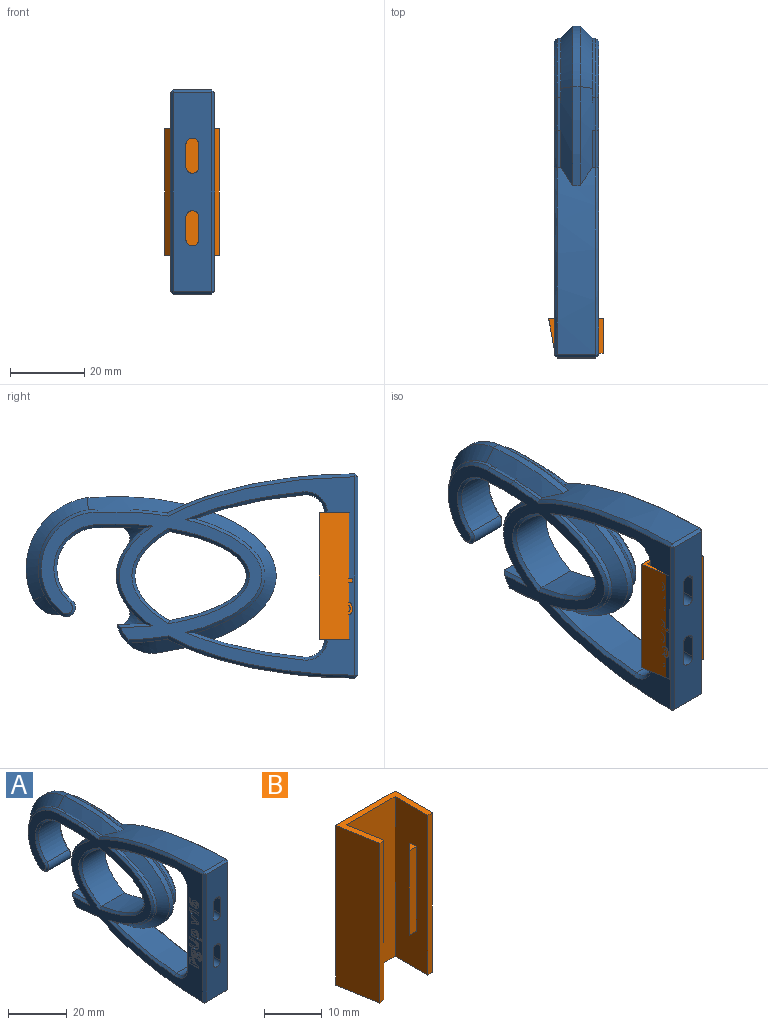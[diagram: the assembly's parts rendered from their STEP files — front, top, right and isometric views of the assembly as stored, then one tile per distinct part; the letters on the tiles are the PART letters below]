
ASSEMBLY  parts=2 mates=1
PART A: 284 faces, bbox 13x92.1x56.1 mm
  f0: plane 85.41x54.41mm, normal (-1,0,0), area 1114.5mm2, adj f78,f79,f80,f81,f82,f83,f84,f85
  f1: cylinder r=16mm len=28.43mm, axis (-1,0,0), area 47.1mm2, adj f12,f14,f65,f66,f70,f76,f105
  f2: extruded ~10.08x1.04mm, area 9.1mm2, adj f14,f16,f70,f101
  f3: extruded ~10.91x4.2mm, area 19mm2, adj f17,f19,f62,f63,f100
  f4: extruded ~30.7x18.87mm, area 61.6mm2, adj f8,f11,f48,f114
  f5: plane 33.72x10.4mm, normal (0,1,0), area 99mm2, adj f9,f10,f35,f37,f38,f39,f40,f41
  f6: plane 53.4x10.4mm, normal (0,-1,0), area 494.1mm2, adj f27,f28,f29,f30,f31,f32,f33,f34
  f7: extruded ~24x11.2mm, area 354.4mm2, adj f25,f26,f122
  f8: extruded ~29.4x10.4mm, area 288mm2, adj f4,f9,f23,f47,f48,f49,f115,f119
  f9: cylinder r=5mm len=10.4mm, axis (-1,0,0), area 85.2mm2, adj f5,f8,f43,f113,f121
  f10: cylinder r=5mm len=10.4mm, axis (-1,0,0), area 85.2mm2, adj f5,f11,f36,f110,f118
  f11: extruded ~29.4x10.4mm, area 288mm2, adj f4,f10,f23,f47,f48,f49,f112,f116
  f12: cylinder r=2.5mm len=10.4mm, axis (-1,0,0), area 81.7mm2, adj f1,f13,f24,f72,f81,f107
  f13: cylinder r=16mm len=28.43mm, axis (-1,0,0), area 47.1mm2, adj f12,f14,f67,f68,f71,f77,f83
  f14: plane 10.41x8.77mm, normal (0,0,1), area 80.5mm2, adj f1,f2,f13,f15,f70,f71,f75,f85
  f15: extruded ~10.08x1.04mm, area 9.1mm2, adj f14,f16,f71,f87
  f16: extruded ~50.36x10.53mm, area 511.9mm2, adj f2,f15,f69,f70,f71,f90,f95,f99
  f17: extruded ~50.36x10.53mm, area 511.8mm2, adj f3,f18,f60,f62,f64,f88,f93,f98
  f18: extruded ~10.91x4.2mm, area 19mm2, adj f17,f19,f60,f61,f86
  f19: cylinder r=9.71mm len=10.76mm, axis (-1,0,0), area 76.6mm2, adj f3,f18,f20,f61,f63,f64,f84,f102
  f20: extruded ~10.4x7.29mm, area 38.9mm2, adj f19,f21,f55,f56,f57,f58,f59,f82
  f21: extruded ~25.66x10.4mm, area 250.9mm2, adj f20,f22,f50,f51,f52,f53,f54,f55
  f22: extruded ~13.86x10.4mm, area 107.3mm2, adj f21,f24,f50,f51,f52,f53,f54,f78
  f23: extruded ~30.7x18.87mm, area 61.6mm2, adj f8,f11,f47,f117
  f24: cylinder r=11mm len=19.46mm, axis (-1,0,0), area 267.4mm2, adj f12,f22,f79,f109
  f25: extruded ~24x20.76mm, area 570.7mm2, adj f7,f26,f123
  f26: plane 85.41x54.41mm, normal (1,0,0), area 1216.5mm2, adj f7,f25,f94,f98,f99,f100,f101,f102
  f27: cylinder r=1.75mm len=6mm, axis (0,-1,0), area 33mm2, adj f6,f28,f30,f44
  f28: plane 6x6mm, normal (1,0,0), area 36mm2, adj f6,f27,f29,f42
  f29: cylinder r=1.75mm len=6mm, axis (0,-1,0), area 33mm2, adj f6,f28,f30,f41,f43,f45
  f30: plane 6x6mm, normal (-1,0,0), area 36mm2, adj f6,f27,f29,f46
  f31: plane 6x6mm, normal (-1,0,0), area 36mm2, adj f6,f32,f34,f40
  f32: cylinder r=1.75mm len=6mm, axis (0,-1,0), area 33mm2, adj f6,f31,f33,f35,f36,f38
  f33: plane 6x6mm, normal (1,0,0), area 36mm2, adj f6,f32,f34,f37
  f34: cylinder r=1.75mm len=6mm, axis (0,-1,0), area 33mm2, adj f6,f31,f33,f39
  f35: cone r=4.75mm half-angle=45deg, axis (0,1,0), area 14.4mm2, adj f5,f32,f36,f37
  f36: bspline ~4.77x3.13mm, area 13.8mm2, adj f10,f32,f35,f38
  f37: plane 6x3mm, normal (0.71,0.71,0), area 25.5mm2, adj f5,f33,f35,f39
  f38: cone r=4.75mm half-angle=45deg, axis (0,1,0), area 14.4mm2, adj f5,f32,f36,f40
  f39: cone r=4.75mm half-angle=45deg, axis (0,1,0), area 43.3mm2, adj f5,f34,f37,f40
  f40: plane 6x3mm, normal (-0.71,0.71,0), area 25.5mm2, adj f5,f31,f38,f39
  f41: cone r=4.75mm half-angle=45deg, axis (0,1,0), area 14.4mm2, adj f5,f29,f42,f43
  f42: plane 6x3mm, normal (0.71,0.71,0), area 25.5mm2, adj f5,f28,f41,f44
  f43: bspline ~4.77x3.13mm, area 13.8mm2, adj f9,f29,f41,f45
  f44: cone r=4.75mm half-angle=45deg, axis (0,1,0), area 43.3mm2, adj f5,f27,f42,f46
  f45: cone r=4.75mm half-angle=45deg, axis (0,1,0), area 14.4mm2, adj f5,f29,f43,f46
  f46: plane 6x3mm, normal (-0.71,0.71,0), area 25.5mm2, adj f5,f30,f44,f45
  f47: bspline ~40.67x32.57mm, area 230mm2, adj f8,f11,f23,f49
  f48: bspline ~40.67x32.57mm, area 230mm2, adj f4,f8,f11,f49
  f49: extruded ~34.16x17.06mm, area 102.3mm2, adj f8,f11,f47,f48
  f50: cone r=3mm half-angle=45deg, axis (1,0,0), area 12.9mm2, adj f21,f22,f51,f54
  f51: plane 0.41x0.27mm, normal (1,0,0), area 0.1mm2, adj f21,f22,f50
  f52: cone r=7mm half-angle=45deg, axis (-1,0,0), area 12.9mm2, adj f21,f22,f53,f54
  f53: plane 0.41x0.27mm, normal (-1,0,0), area 0.1mm2, adj f21,f22,f52
  f54: cylinder r=3mm len=4.8mm, axis (-1,0,0), area 13.2mm2, adj f21,f22,f50,f52
  f55: cone r=3mm half-angle=45deg, axis (1,0,0), area 12.9mm2, adj f20,f21,f56,f59
  f56: plane 0.41x0.27mm, normal (1,0,0), area 0.1mm2, adj f20,f21,f55
  f57: cone r=7mm half-angle=45deg, axis (-1,0,0), area 12.9mm2, adj f20,f21,f58,f59
  f58: plane 0.41x0.27mm, normal (-1,0,0), area 0.1mm2, adj f20,f21,f57
  f59: cylinder r=3mm len=4.8mm, axis (-1,0,0), area 13.2mm2, adj f20,f21,f55,f57
  f60: bspline ~14.46x6.99mm, area 25.7mm2, adj f17,f18,f61,f64
  f61: cone r=9.71mm half-angle=45deg, axis (1,0,0), area 18.1mm2, adj f18,f19,f60
  f62: bspline ~14.46x6.99mm, area 25.7mm2, adj f3,f17,f63,f64
  f63: cone r=5.71mm half-angle=45deg, axis (-1,0,0), area 18.1mm2, adj f3,f19,f62
  f64: extruded ~7.7x2mm, area 15.7mm2, adj f17,f19,f60,f62
  f65: cone r=15.27mm half-angle=45deg, axis (-1,0,0), area 153mm2, adj f1,f66,f70,f74
  f66: cone r=3mm half-angle=45deg, axis (-1,0,0), area 22.6mm2, adj f1,f65,f73,f76
  f67: cone r=19.27mm half-angle=45deg, axis (1,0,0), area 153mm2, adj f13,f68,f71,f74
  f68: cone r=7mm half-angle=45deg, axis (1,0,0), area 22.6mm2, adj f13,f67,f73,f77
  f69: extruded ~26.57x2.12mm, area 53.5mm2, adj f16,f70,f71,f74
  f70: bspline ~38.15x7.96mm, area 112.2mm2, adj f1,f2,f14,f16,f65,f69,f75
  f71: bspline ~38.15x7.96mm, area 112.2mm2, adj f13,f14,f15,f16,f67,f69,f75
  f72: plane 2x0.93mm, normal (0,0,-1), area 1.9mm2, adj f12,f73,f76,f77
  f73: cylinder r=7mm len=6.28mm, axis (-1,0,0), area 15.6mm2, adj f66,f68,f72,f74
  f74: cylinder r=19.27mm len=27.58mm, axis (-1,0,0), area 72.4mm2, adj f65,f67,f69,f73
  f75: extruded ~8.66x7.52mm, area 65.2mm2, adj f14,f70,f71
  f76: plane 0.95x0.83mm, normal (0.71,0,-0.71), area 0.5mm2, adj f1,f66,f72
  f77: plane 0.95x0.83mm, normal (-0.71,0,-0.71), area 0.5mm2, adj f13,f68,f72
  f78: bspline ~16.07x1.3mm, area 16.9mm2, adj f0,f22,f79,f80
  f79: cone r=11.8mm half-angle=45deg, axis (-1,0,0), area 30.2mm2, adj f0,f24,f78,f81
  f80: bspline ~30.07x11.02mm, area 36.3mm2, adj f0,f21,f78,f82
  f81: cone r=2.5mm half-angle=45deg, axis (1,0,0), area 7.5mm2, adj f0,f12,f79,f83
  f82: bspline ~10.35x1.36mm, area 8.9mm2, adj f0,f20,f80,f84
  f83: cone r=16mm half-angle=45deg, axis (1,0,0), area 43.4mm2, adj f0,f13,f81,f85
  f84: cone r=9.71mm half-angle=45deg, axis (1,0,0), area 5.4mm2, adj f0,f19,f82,f86
  f85: plane 8.76x0.8mm, normal (-0.71,0,0.71), area 9.9mm2, adj f0,f14,f83,f87
  f86: bspline ~11.21x1.9mm, area 12.3mm2, adj f0,f18,f84,f88
  f87: bspline ~10.39x1.87mm, area 11.6mm2, adj f0,f15,f85,f90
  f88: bspline ~55.49x12.73mm, area 58.6mm2, adj f0,f17,f86,f91
  f89: plane 53.4x0.8mm, normal (-0.71,-0.71,0), area 60.4mm2, adj f0,f6,f91,f92
  f90: bspline ~55.49x12.73mm, area 58.6mm2, adj f0,f16,f87,f92
  f91: plane 0.8x0.8mm, normal (-0.58,-0.58,-0.58), area 0.6mm2, adj f88,f89,f93
  f92: plane 0.8x0.8mm, normal (-0.58,-0.58,0.58), area 0.6mm2, adj f89,f90,f95
  f93: plane 10.4x0.8mm, normal (0,-0.71,-0.71), area 11.8mm2, adj f6,f17,f91,f96
  f94: plane 53.4x0.8mm, normal (0.71,-0.71,0), area 60.4mm2, adj f6,f26,f96,f97
  f95: plane 10.4x0.8mm, normal (0,-0.71,0.71), area 11.8mm2, adj f6,f16,f92,f97
  f96: plane 0.8x0.8mm, normal (0.58,-0.58,-0.58), area 0.6mm2, adj f93,f94,f98
  f97: plane 0.8x0.8mm, normal (0.58,-0.58,0.58), area 0.6mm2, adj f94,f95,f99
  f98: bspline ~55.49x12.73mm, area 58.6mm2, adj f17,f26,f96,f100
  f99: bspline ~55.49x12.73mm, area 58.6mm2, adj f16,f26,f97,f101
  f100: bspline ~11.21x1.9mm, area 12.3mm2, adj f3,f26,f98,f102
  f101: bspline ~10.39x1.87mm, area 11.6mm2, adj f2,f26,f99,f103
  f102: cone r=8.91mm half-angle=45deg, axis (-1,0,0), area 5.4mm2, adj f19,f26,f100,f104
  f103: plane 8.76x0.8mm, normal (0.71,0,0.71), area 9.9mm2, adj f14,f26,f101,f105
  f104: bspline ~9.42x1.3mm, area 8.9mm2, adj f20,f26,f102,f106
  f105: cone r=15.2mm half-angle=45deg, axis (-1,0,0), area 43.4mm2, adj f1,f26,f103,f107
  f106: bspline ~30.07x11.02mm, area 36.3mm2, adj f21,f26,f104,f108
  f107: cone r=1.7mm half-angle=45deg, axis (-1,0,0), area 7.5mm2, adj f12,f26,f105,f109
  f108: bspline ~16.07x1.3mm, area 16.9mm2, adj f22,f26,f106,f109
  f109: cone r=11mm half-angle=45deg, axis (1,0,0), area 30.2mm2, adj f24,f26,f107,f108
  f110: cone r=5mm half-angle=45deg, axis (1,0,0), area 10.2mm2, adj f10,f26,f111,f112
  f111: plane 33.72x0.8mm, normal (0.71,0.71,0), area 38.1mm2, adj f5,f26,f110,f113
  f112: bspline ~31.88x8.19mm, area 35.6mm2, adj f11,f26,f110,f114
  f113: cone r=5.8mm half-angle=45deg, axis (1,0,0), area 10.2mm2, adj f9,f26,f111,f115
  f114: bspline ~31.9x21.32mm, area 60mm2, adj f4,f26,f112,f115
  f115: bspline ~33.39x8.89mm, area 35.7mm2, adj f8,f26,f113,f114
  f116: bspline ~33.36x8.88mm, area 35.6mm2, adj f0,f11,f117,f118
  f117: bspline ~33.07x23.99mm, area 60mm2, adj f0,f23,f116,f119
  f118: cone r=5.8mm half-angle=45deg, axis (-1,0,0), area 10.2mm2, adj f0,f10,f116,f120
  f119: bspline ~33.39x8.89mm, area 35.7mm2, adj f0,f8,f117,f121
  f120: plane 33.72x0.8mm, normal (-0.71,0.71,0), area 38.1mm2, adj f0,f5,f118,f121
  f121: cone r=5mm half-angle=45deg, axis (-1,0,0), area 10.2mm2, adj f0,f9,f119,f120
  f122: bspline ~27.31x11.74mm, area 37.1mm2, adj f0,f7,f123
  f123: bspline ~26.44x24.47mm, area 59.3mm2, adj f0,f25,f122
  f124: plane 2.89x0.3mm, normal (0,0,-1), area 0.9mm2, adj f0,f125,f138,f139
  f125: plane 0.94x0.3mm, normal (0,-1,0), area 0.3mm2, adj f0,f124,f126,f139
  f126: plane 2.73x0.3mm, normal (0,0,1), area 0.8mm2, adj f0,f125,f127,f139
  f127: extruded ~0.76x0.3mm, area 0.2mm2, adj f0,f126,f128,f139
  f128: extruded ~0.67x0.3mm, area 0.2mm2, adj f0,f127,f129,f139
  f129: extruded ~0.69x0.3mm, area 0.2mm2, adj f0,f128,f130,f139
  f130: extruded ~0.76x0.3mm, area 0.2mm2, adj f0,f129,f131,f139
  f131: plane 2.73x0.3mm, normal (0,0,-1), area 0.8mm2, adj f0,f130,f132,f139
  f132: plane 0.94x0.3mm, normal (0,-1,0), area 0.3mm2, adj f0,f131,f133,f139
  f133: plane 2.88x0.3mm, normal (0,0,1), area 0.9mm2, adj f0,f132,f134,f139
  f134: extruded ~1.21x0.48mm, area 0.4mm2, adj f0,f133,f135,f139
  f135: extruded ~1.34x0.44mm, area 0.4mm2, adj f0,f134,f136,f139
  f136: extruded ~0.99x0.3mm, area 0.3mm2, adj f0,f135,f137,f139
  f137: extruded ~0.64x0.57mm, area 0.3mm2, adj f0,f136,f138,f139
  f138: extruded ~0.87x0.3mm, area 0.3mm2, adj f0,f124,f137,f139
  f139: plane 4.52x3.66mm, normal (-1,0,0), area 9.1mm2, adj f124,f125,f126,f127,f128,f129,f130,f131
  f140: extruded ~0.44x0.3mm, area 0.1mm2, adj f141,f183,f184,f276
  f141: extruded ~0.62x0.51mm, area 0.3mm2, adj f140,f142,f184,f276
  f142: extruded ~0.62x0.51mm, area 0.3mm2, adj f141,f143,f184,f276
  f143: extruded ~0.44x0.3mm, area 0.1mm2, adj f142,f144,f184,f276
  f144: extruded ~0.38x0.3mm, area 0.1mm2, adj f143,f183,f184,f276
  f145: extruded ~0.3x0.3mm, area 0.1mm2, adj f146,f181,f184,f185
  f146: extruded ~0.32x0.3mm, area 0.1mm2, adj f145,f147,f184,f185
  f147: extruded ~0.43x0.3mm, area 0.1mm2, adj f146,f148,f184,f185
  f148: plane 0.48x0.3mm, normal (0,1,0), area 0.1mm2, adj f147,f149,f184,f185
  f149: extruded ~0.52x0.3mm, area 0.2mm2, adj f148,f150,f184,f185
  f150: extruded ~0.3x0.27mm, area 0.1mm2, adj f149,f151,f184,f185
  f151: extruded ~0.38x0.3mm, area 0.1mm2, adj f150,f152,f184,f185
  f152: extruded ~0.78x0.3mm, area 0.2mm2, adj f151,f181,f184,f185
  f153: plane 0.47x0.3mm, normal (0,0,-1), area 0.1mm2, adj f0,f154,f182,f184
  f154: plane 1.19x0.3mm, normal (0,-1,0), area 0.4mm2, adj f0,f153,f155,f184
  f155: extruded ~0.3x0.25mm, area 0.1mm2, adj f0,f154,f156,f184
  f156: extruded ~0.34x0.3mm, area 0.1mm2, adj f0,f155,f157,f184
  f157: extruded ~1.04x0.31mm, area 0.3mm2, adj f0,f156,f158,f184
  f158: extruded ~0.86x0.36mm, area 0.3mm2, adj f0,f157,f159,f184
  f159: extruded ~0.61x0.3mm, area 0.2mm2, adj f0,f158,f160,f184
  f160: extruded ~0.43x0.37mm, area 0.2mm2, adj f0,f159,f161,f184
  f161: extruded ~0.33x0.3mm, area 0.1mm2, adj f0,f160,f162,f184
  f162: extruded ~0.32x0.3mm, area 0.1mm2, adj f0,f161,f163,f184
  f163: extruded ~0.3x0.3mm, area 0.1mm2, adj f0,f162,f164,f184
  f164: extruded ~0.3x0.25mm, area 0.1mm2, adj f0,f163,f165,f184
  f165: extruded ~0.56x0.3mm, area 0.2mm2, adj f0,f164,f166,f184
  f166: extruded ~0.52x0.3mm, area 0.2mm2, adj f0,f165,f167,f184
  f167: extruded ~0.7x0.38mm, area 0.2mm2, adj f0,f166,f168,f184
  f168: extruded ~1.09x0.3mm, area 0.3mm2, adj f0,f167,f169,f184
  f169: extruded ~1.43x0.33mm, area 0.4mm2, adj f0,f168,f170,f184
  f170: extruded ~0.93x0.5mm, area 0.3mm2, adj f0,f169,f171,f184
  f171: extruded ~0.71x0.3mm, area 0.2mm2, adj f0,f170,f172,f184
  f172: extruded ~0.86x0.3mm, area 0.3mm2, adj f0,f171,f173,f184
  f173: plane 0.58x0.3mm, normal (0,-1,0), area 0.2mm2, adj f0,f172,f174,f184
  f174: extruded ~0.51x0.3mm, area 0.2mm2, adj f0,f173,f175,f184
  f175: extruded ~0.3x0.24mm, area 0.1mm2, adj f0,f174,f176,f184
  f176: plane 0.3x0.14mm, normal (0,0.99,0.11), area 0mm2, adj f0,f175,f177,f184
  f177: plane 0.3x0.17mm, normal (0,1,0.06), area 0.1mm2, adj f0,f176,f178,f184
  f178: extruded ~1.06x0.31mm, area 0.3mm2, adj f0,f177,f179,f184
  f179: extruded ~0.86x0.38mm, area 0.3mm2, adj f0,f178,f180,f184
  f180: extruded ~0.51x0.3mm, area 0.2mm2, adj f0,f179,f182,f184
  f181: extruded ~0.52x0.3mm, area 0.2mm2, adj f145,f152,f184,f185
  f182: plane 0.53x0.3mm, normal (0,0.97,-0.25), area 0.2mm2, adj f0,f153,f180,f184
  f183: extruded ~0.39x0.3mm, area 0.1mm2, adj f140,f144,f184,f276
  f184: plane 4.98x3.44mm, normal (-1,0,0), area 10.1mm2, adj f140,f141,f142,f143,f144,f145,f146,f147
  f185: plane 1.77x0.85mm, normal (-1,0,0), area 1.3mm2, adj f145,f146,f147,f148,f149,f150,f151,f152
  f186: extruded ~0.46x0.3mm, area 0.2mm2, adj f187,f210,f211,f277
  f187: extruded ~0.48x0.3mm, area 0.2mm2, adj f186,f188,f211,f277
  f188: extruded ~0.61x0.3mm, area 0.2mm2, adj f187,f189,f211,f277
  f189: extruded ~0.43x0.3mm, area 0.1mm2, adj f188,f190,f211,f277
  f190: extruded ~0.49x0.3mm, area 0.2mm2, adj f189,f191,f211,f277
  f191: extruded ~0.46x0.3mm, area 0.2mm2, adj f190,f192,f211,f277
  f192: extruded ~0.51x0.3mm, area 0.2mm2, adj f191,f210,f211,f277
  f193: extruded ~1.97x0.56mm, area 0.6mm2, adj f0,f194,f209,f211
  f194: extruded ~1.06x0.3mm, area 0.3mm2, adj f0,f193,f195,f211
  f195: extruded ~0.67x0.57mm, area 0.3mm2, adj f0,f194,f196,f211
  f196: extruded ~0.86x0.3mm, area 0.3mm2, adj f0,f195,f197,f211
  f197: extruded ~1.12x0.42mm, area 0.4mm2, adj f0,f196,f198,f211
  f198: extruded ~1.13x0.4mm, area 0.4mm2, adj f0,f197,f199,f211
  f199: extruded ~1.04x0.34mm, area 0.3mm2, adj f0,f198,f200,f211
  f200: extruded ~0.94x0.38mm, area 0.3mm2, adj f0,f199,f201,f211
  f201: extruded ~0.97x0.52mm, area 0.3mm2, adj f0,f200,f202,f211
  f202: plane 0.3x0.04mm, normal (0,-1,0), area 0mm2, adj f0,f201,f203,f211
  f203: extruded ~0.81x0.3mm, area 0.3mm2, adj f0,f202,f204,f211
  f204: extruded ~0.46x0.43mm, area 0.2mm2, adj f0,f203,f205,f211
  f205: extruded ~0.79x0.3mm, area 0.2mm2, adj f0,f204,f206,f211
  f206: extruded ~0.54x0.3mm, area 0.2mm2, adj f0,f205,f207,f211
  f207: plane 0.75x0.3mm, normal (0,0,-1), area 0.2mm2, adj f0,f206,f208,f211
  f208: extruded ~0.6x0.3mm, area 0.2mm2, adj f0,f207,f209,f211
  f209: extruded ~1.68x0.65mm, area 0.6mm2, adj f0,f193,f208,f211
  f210: extruded ~0.58x0.3mm, area 0.2mm2, adj f186,f192,f211,f277
  f211: plane 4.58x3.15mm, normal (-1,0,0), area 8.5mm2, adj f186,f187,f188,f189,f190,f191,f192,f193
  f212: extruded ~0.5x0.3mm, area 0.2mm2, adj f213,f234,f235,f278
  f213: extruded ~0.48x0.3mm, area 0.2mm2, adj f212,f214,f235,f278
  f214: extruded ~0.76x0.3mm, area 0.2mm2, adj f213,f215,f235,f278
  f215: extruded ~1.03x0.63mm, area 0.4mm2, adj f214,f216,f235,f278
  f216: extruded ~0.52x0.3mm, area 0.2mm2, adj f215,f217,f235,f278
  f217: extruded ~0.79x0.3mm, area 0.2mm2, adj f216,f218,f235,f278
  f218: plane 0.3x0.1mm, normal (0,0,-1), area 0mm2, adj f217,f234,f235,f278
  f219: extruded ~0.94x0.44mm, area 0.3mm2, adj f0,f220,f233,f235
  f220: extruded ~0.7x0.3mm, area 0.2mm2, adj f0,f219,f221,f235
  f221: extruded ~0.61x0.46mm, area 0.2mm2, adj f0,f220,f222,f235
  f222: extruded ~0.95x0.3mm, area 0.3mm2, adj f0,f221,f223,f235
  f223: extruded ~1.3x0.34mm, area 0.4mm2, adj f0,f222,f224,f235
  f224: extruded ~0.95x0.47mm, area 0.3mm2, adj f0,f223,f225,f235
  f225: extruded ~0.97x0.51mm, area 0.3mm2, adj f0,f224,f226,f235
  f226: plane 0.3x0.04mm, normal (0,-1,0), area 0mm2, adj f0,f225,f227,f235
  f227: plane 0.44x0.3mm, normal (0,-0.28,-0.96), area 0.1mm2, adj f0,f226,f228,f235
  f228: plane 0.76x0.3mm, normal (0,-1,0), area 0.2mm2, adj f0,f227,f229,f235
  f229: plane 4.91x0.3mm, normal (0,0,1), area 1.5mm2, adj f0,f228,f230,f235
  f230: plane 0.93x0.3mm, normal (0,1,0), area 0.3mm2, adj f0,f229,f231,f235
  f231: plane 1.38x0.3mm, normal (0,0,-1), area 0.4mm2, adj f0,f230,f232,f235
  f232: extruded ~0.49x0.3mm, area 0.1mm2, adj f0,f231,f233,f235
  f233: plane 0.3x0.05mm, normal (0,1,0), area 0mm2, adj f0,f219,f232,f235
  f234: extruded ~0.7x0.3mm, area 0.2mm2, adj f212,f218,f235,f278
  f235: plane 4.98x3.19mm, normal (-1,0,0), area 9.1mm2, adj f212,f213,f214,f215,f216,f217,f218,f219
  f236: extruded ~1.1x0.45mm, area 0.4mm2, adj f0,f237,f251,f252
  f237: extruded ~1.04x0.42mm, area 0.3mm2, adj f0,f236,f238,f252
  f238: extruded ~1.24x0.35mm, area 0.4mm2, adj f0,f237,f239,f252
  f239: plane 1.43x0.3mm, normal (0,-1,0), area 0.4mm2, adj f0,f238,f240,f252
  f240: plane 4.46x0.3mm, normal (0,0,1), area 1.3mm2, adj f0,f239,f241,f252
  f241: plane 0.95x0.3mm, normal (0,1,0), area 0.3mm2, adj f0,f240,f242,f252
  f242: plane 1.59x0.3mm, normal (0,0,-1), area 0.5mm2, adj f0,f241,f243,f252
  f243: plane 0.41x0.3mm, normal (0,1,0), area 0.1mm2, adj f0,f242,f251,f252
  f244: plane 0.31x0.3mm, normal (0,-1,0), area 0.1mm2, adj f245,f250,f252,f253
  f245: plane 1.32x0.3mm, normal (0,0,-1), area 0.4mm2, adj f244,f246,f252,f253
  f246: plane 0.43x0.3mm, normal (0,1,0), area 0.1mm2, adj f245,f247,f252,f253
  f247: extruded ~0.57x0.3mm, area 0.2mm2, adj f246,f248,f252,f253
  f248: extruded ~0.49x0.3mm, area 0.2mm2, adj f247,f249,f252,f253
  f249: extruded ~0.5x0.3mm, area 0.2mm2, adj f248,f250,f252,f253
  f250: extruded ~0.65x0.3mm, area 0.2mm2, adj f244,f249,f252,f253
  f251: extruded ~1.28x0.38mm, area 0.4mm2, adj f0,f236,f243,f252
  f252: plane 4.46x3.08mm, normal (-1,0,0), area 8.1mm2, adj f236,f237,f238,f239,f240,f241,f242,f243
  f253: plane 1.32x1.18mm, normal (-1,0,0), area 1.4mm2, adj f244,f245,f246,f247,f248,f249,f250
  f254: plane 0.94x0.3mm, normal (0,1,0), area 0.3mm2, adj f0,f255,f263,f264
  f255: plane 4.46x0.3mm, normal (0,0,-1), area 1.3mm2, adj f0,f254,f256,f264
  f256: plane 0.78x0.3mm, normal (0,-1,0), area 0.2mm2, adj f0,f255,f257,f264
  f257: plane 1.44x1.14mm, normal (0,-0.78,0.62), area 0.6mm2, adj f0,f256,f258,f264
  f258: plane 0.57x0.46mm, normal (0,0.63,0.78), area 0.2mm2, adj f0,f257,f259,f264
  f259: plane 0.51x0.41mm, normal (0,0.78,-0.63), area 0.2mm2, adj f0,f258,f260,f264
  f260: extruded ~0.33x0.31mm, area 0.1mm2, adj f0,f259,f261,f264
  f261: plane 0.46x0.3mm, normal (0,-0.03,1), area 0.1mm2, adj f0,f260,f262,f264
  f262: plane 0.42x0.3mm, normal (0,-0.02,1), area 0.1mm2, adj f0,f261,f263,f264
  f263: plane 2.58x0.3mm, normal (0,0,1), area 0.8mm2, adj f0,f254,f262,f264
  f264: plane 4.46x2.21mm, normal (-1,0,0), area 5.1mm2, adj f254,f255,f256,f257,f258,f259,f260,f261
  f265: plane 3.41x1.3mm, normal (0,0.36,0.93), area 1.1mm2, adj f0,f266,f274,f275
  f266: plane 0.96x0.3mm, normal (0,1,0), area 0.3mm2, adj f0,f265,f267,f275
  f267: plane 3.41x1.3mm, normal (0,0.36,-0.93), area 1.1mm2, adj f0,f266,f268,f275
  f268: plane 0.97x0.3mm, normal (0,-1,0), area 0.3mm2, adj f0,f267,f269,f275
  f269: plane 1.94x0.66mm, normal (0,-0.32,0.95), area 0.6mm2, adj f0,f268,f270,f275
  f270: extruded ~0.7x0.3mm, area 0.2mm2, adj f0,f269,f271,f275
  f271: plane 0.3x0.02mm, normal (0,-1,0), area 0mm2, adj f0,f270,f272,f275
  f272: extruded ~0.7x0.3mm, area 0.2mm2, adj f0,f271,f273,f275
  f273: plane 1.94x0.66mm, normal (0,-0.32,-0.95), area 0.6mm2, adj f0,f272,f274,f275
  f274: plane 0.97x0.3mm, normal (0,-1,0), area 0.3mm2, adj f0,f265,f273,f275
  f275: plane 3.56x3.41mm, normal (-1,0,0), area 5.8mm2, adj f265,f266,f267,f268,f269,f270,f271,f272
  f276: plane 1.22x1.02mm, normal (-1,0,0), area 1mm2, adj f140,f141,f142,f143,f144,f183
  f277: plane 1.48x1.3mm, normal (-1,0,0), area 1.6mm2, adj f186,f187,f188,f189,f190,f191,f192,f210
  f278: plane 2.04x1.31mm, normal (-1,0,0), area 2.2mm2, adj f212,f213,f214,f215,f216,f217,f218,f234
  f279: cylinder r=1mm len=2mm, axis (1,0,0), area 6.3mm2, adj f26,f280,f282,f283
  f280: plane 18x2mm, normal (0,1,0), area 36mm2, adj f26,f279,f281,f283
  f281: cylinder r=1mm len=2mm, axis (1,0,0), area 6.3mm2, adj f26,f280,f282,f283
  f282: plane 18x2mm, normal (0,-1,0), area 36mm2, adj f26,f279,f281,f283
  f283: plane 20x2mm, normal (1,0,0), area 39.1mm2, adj f279,f280,f281,f282
PART B: 15 faces, bbox 14.6x9.3x34 mm
  f0: plane 34x8mm, normal (-1,0,0), area 245mm2, adj f1,f2,f4,f9,f10,f11,f12,f13
  f1: plane 34x1.2mm, normal (0,-1,0), area 40.8mm2, adj f0,f2,f4,f7
  f2: plane 14.63x9.29mm, normal (0,0,-1), area 36.8mm2, adj f0,f1,f3,f5,f6,f7,f8,f9
  f3: plane 34x1.18mm, normal (0.17,-0.98,0), area 40.8mm2, adj f2,f4,f5,f8
  f4: plane 14.63x9.29mm, normal (0,0,1), area 36.8mm2, adj f0,f1,f3,f5,f6,f7,f8,f9
  f5: plane 34x9.29mm, normal (-0.98,-0.17,0), area 320.6mm2, adj f2,f3,f4,f6
  f6: plane 34x14.63mm, normal (0,1,0), area 497.4mm2, adj f2,f4,f5,f7
  f7: plane 34x9.2mm, normal (1,0,0), area 312.8mm2, adj f1,f2,f4,f6
  f8: plane 34x7.88mm, normal (0.98,0.17,0), area 272mm2, adj f2,f3,f4,f9
  f9: plane 34x12mm, normal (0,-1,0), area 408mm2, adj f0,f2,f4,f8
  f10: plane 18x0.3mm, normal (0,1,0), area 5.4mm2, adj f0,f11,f13,f14
  f11: plane 1.8x1.5mm, normal (0,0,1), area 1.6mm2, adj f0,f10,f12,f14
  f12: plane 18x1.8mm, normal (0,-1,0), area 32.4mm2, adj f0,f11,f13,f14
  f13: plane 1.8x1.5mm, normal (0,0,-1), area 1.6mm2, adj f0,f10,f12,f14
  f14: plane 18x1.5mm, normal (-0.71,0.71,0), area 38.2mm2, adj f10,f11,f12,f13
PLACE A at identity
PLACE B t=(0,-105.11,-2.5)mm
MATE planar B.f0 <-> A.f26  axis (-1,0,0) through (6,-134.5,-2.5)mm
